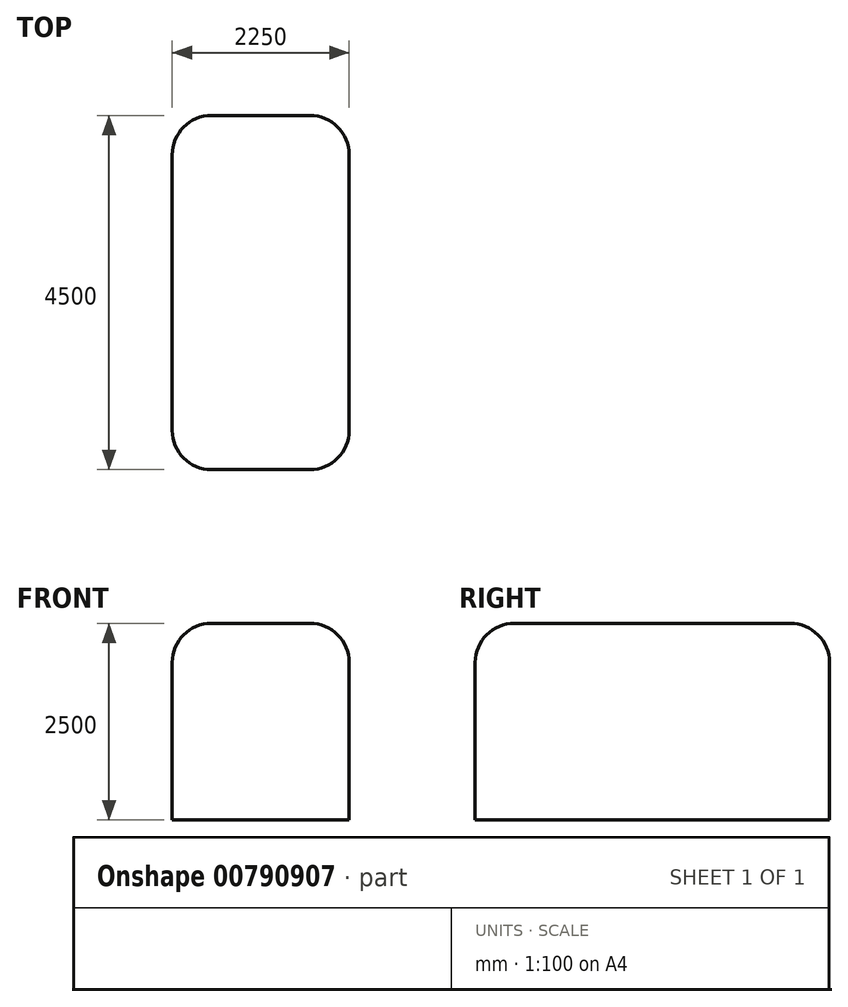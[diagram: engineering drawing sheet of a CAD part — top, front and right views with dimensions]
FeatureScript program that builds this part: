
annotation { "Feature Type Name" : "Feature", "Feature Type Description" : "" }
export const myFeature = defineFeature(function(context is Context, id is Id, definition is map)
    precondition{}
    {
        {
            var Q0;
            Q0=qCreatedBy(makeId("Top.planeOp"),FACE);
            var sketch = newSketch(context, id + "F0", { "sketchPlane" : qUnion([Q0])});
            skLineSegment(sketch, "E0.bottom", {"start": v(0, 0) * mm, "end": v(-2250, 0) * mm});
            skLineSegment(sketch, "E0.top", {"start": v(0, 4500) * mm, "end": v(-2250, 4500) * mm});
            skLineSegment(sketch, "E0.left", {"start": v(0, 0) * mm, "end": v(0, 4500) * mm});
            skLineSegment(sketch, "E0.right", {"start": v(-2250, 0) * mm, "end": v(-2250, 4500) * mm});
            skSolve(sketch);
        }
        {
            var Q0;
            Q0 = qSketchRegion(id + "F0", true);
            extrude(context, id + "F1", {"entities" : qUnion([Q0]), "depth" : 2500 * mm, "offsetDistance" : 25 * mm});
        }
        {
            var Q0;
            Q0=makeQuery(id+"F1.opExtrude","SWEPT_EDGE",EDGE,{"disambiguationData":[OSD([sQuery(id+"F0.wireOp",EDGE,"E0.top"),sQuery(id+"F0.wireOp",EDGE,"E0.right")])]});
            var Q1;
            Q1=makeQuery(id+"F1.opExtrude","SWEPT_EDGE",EDGE,{"disambiguationData":[OSD([sQuery(id+"F0.wireOp",EDGE,"E0.bottom"),sQuery(id+"F0.wireOp",EDGE,"E0.right")])]});
            var Q2;
            Q2=makeQuery(id+"F1.opExtrude","SWEPT_EDGE",EDGE,{"disambiguationData":[OSD([sQuery(id+"F0.wireOp",EDGE,"E0.bottom"),sQuery(id+"F0.wireOp",EDGE,"E0.left")])]});
            var Q3;
            Q3=makeQuery(id+"F1.opExtrude","SWEPT_EDGE",EDGE,{"disambiguationData":[OSD([sQuery(id+"F0.wireOp",EDGE,"E0.top"),sQuery(id+"F0.wireOp",EDGE,"E0.left")])]});
            var Q4;
            Q4=makeQuery(id+"F1.opExtrude","CAP_EDGE",EDGE,{"disambiguationData":[OSD([sQuery(id+"F0.wireOp",EDGE,"E0.right")])],"isStart":false});
            var Q5;
            Q5=makeQuery(id+"F1.opExtrude","CAP_EDGE",EDGE,{"disambiguationData":[OSD([sQuery(id+"F0.wireOp",EDGE,"E0.left")])],"isStart":false});
            var Q6;
            Q6=makeQuery(id+"F1.opExtrude","CAP_EDGE",EDGE,{"disambiguationData":[OSD([sQuery(id+"F0.wireOp",EDGE,"E0.bottom")])],"isStart":false});
            var Q7;
            Q7=makeQuery(id+"F1.opExtrude","CAP_EDGE",EDGE,{"disambiguationData":[OSD([sQuery(id+"F0.wireOp",EDGE,"E0.top")])],"isStart":false});
            fillet(context, id + "F2", {"entities" : qUnion([Q0, Q1, Q2, Q3, Q4, Q5, Q6, Q7]), "radius" : 500 * mm, "tangentPropagation" : true, "allowEdgeOverflow" : false});
        }
    });
